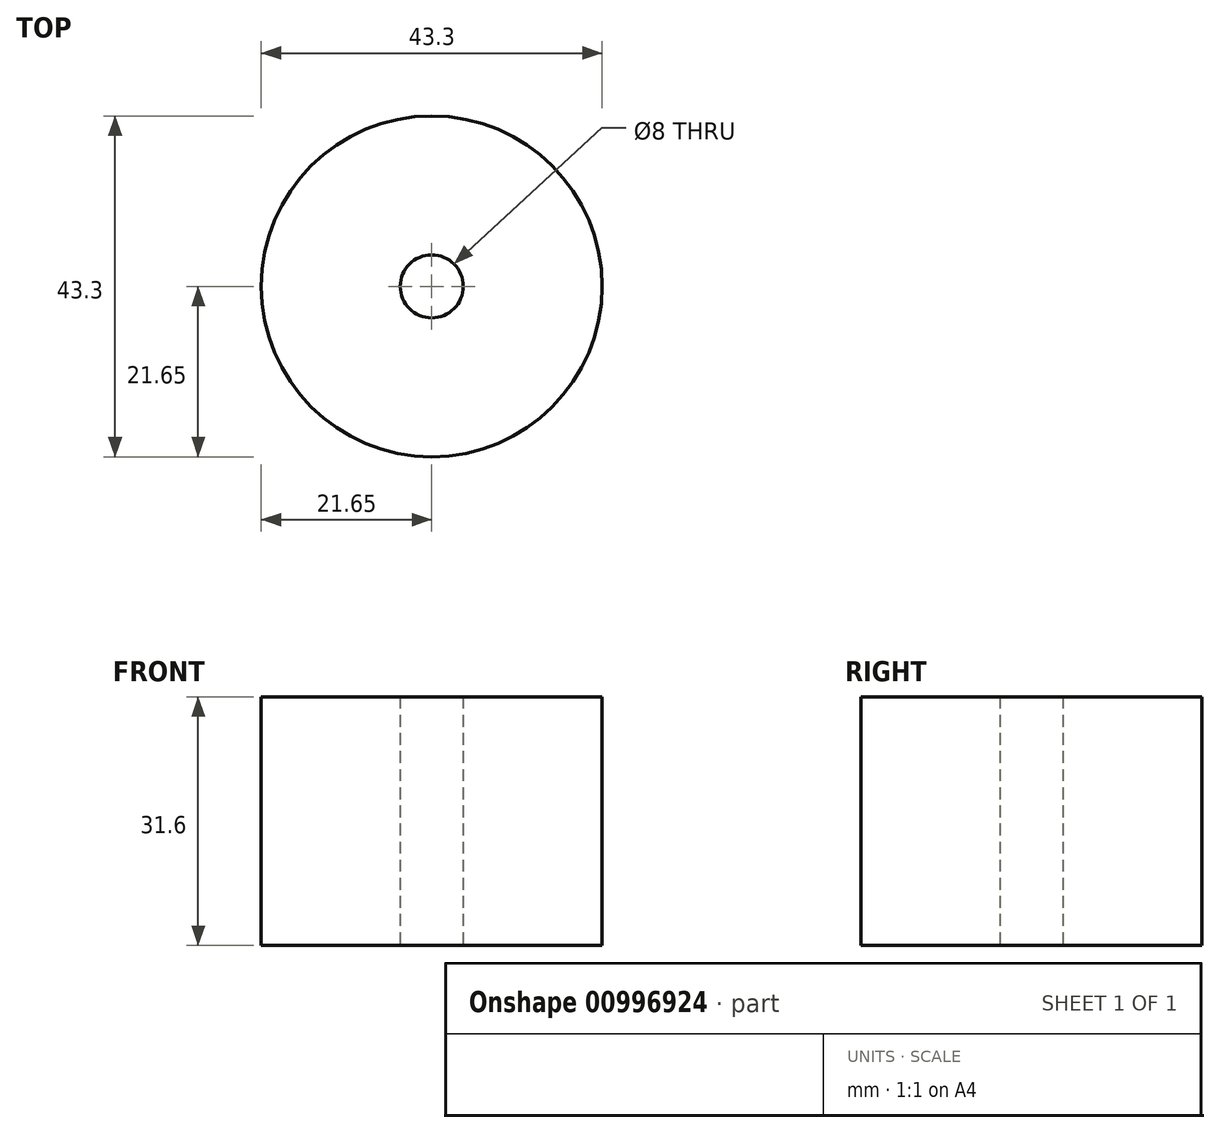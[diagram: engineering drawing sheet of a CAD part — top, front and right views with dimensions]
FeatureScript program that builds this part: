
annotation { "Feature Type Name" : "Feature", "Feature Type Description" : "" }
export const myFeature = defineFeature(function(context is Context, id is Id, definition is map)
    precondition{}
    {
        {
            var Q0;
            Q0=qCreatedBy(makeId("Top.planeOp"),FACE);
            var sketch = newSketch(context, id + "F0", { "sketchPlane" : qUnion([Q0])});
            skCircle(sketch, "E0", {"center": v(0, 0) * mm, "radius": 21.65 * mm});
            skCircle(sketch, "E1", {"center": v(0, 0) * mm, "radius": 4 * mm});
            skSolve(sketch);
        }
        {
            var Q0;
            Q0=makeQuery(id+"F0.imprint","IMPRINT",FACE,{"disambiguationData":[TD([[makeQuery(id+"F0.imprint","IMPRINT",EDGE,{"derivedFrom":sQuery(id+"F0.wireOp",EDGE,"E0")}),1.0]])]});
            var Q1;
            Q1=sQuery(id+"F0.wireOp",EDGE,"E0");
            extrude(context, id + "F1", {"entities" : qUnion([Q0]), "surfaceEntities" : qUnion([Q1]), "depth" : 31.6 * mm, "offsetDistance" : 25 * mm});
        }
    });
